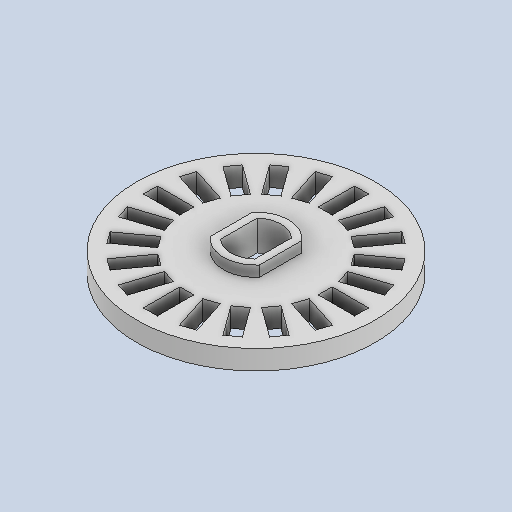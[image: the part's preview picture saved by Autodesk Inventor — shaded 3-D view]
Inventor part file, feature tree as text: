
AUTODESK INVENTOR PART (.ipt)
format: ipt  version: 2022 (Build 260153070, 153G)  size: 243,200 bytes
history: native  units: in
note: dims shown in document units (in); Inventor stores cm internally (conversion verified against a paired STEP export)
features: other x3, sketch x2
ambient origin geometry x8: Origin, YZ Plane, XZ Plane, XY Plane, X Axis, Y Axis, Z Axis, Center Point
bodies: Solid1 (feature_tree)
feature tree (5):
  other  "TT encoder disk.ipt"
  other  "Solid1::TT encoder disk.ipt"
  other  "TaggingFeature1"
  sketch  "Sketch1"  dims[d0=0.3937in]
  sketch  "Sketch2"
